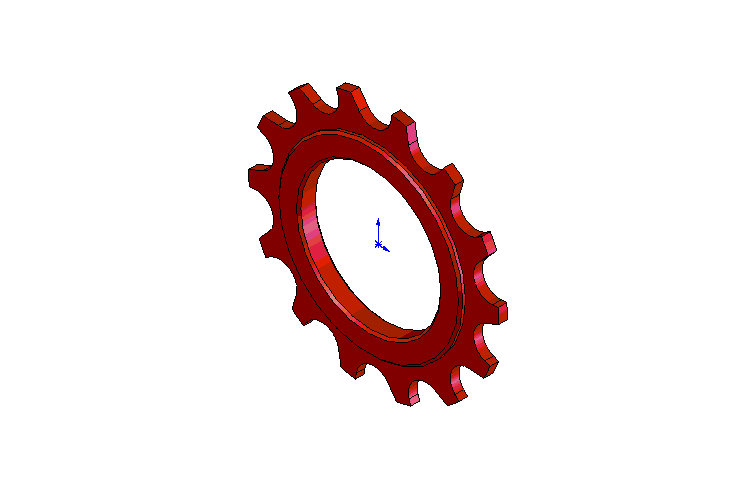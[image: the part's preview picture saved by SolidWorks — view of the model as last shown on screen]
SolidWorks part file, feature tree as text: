
SOLIDWORKS PART (.sldprt)
format: sldprt  version: not decoded by parser v0  size: 244,736 bytes
history: native  units: mm
features: sketch x4, plane x3, extrude x3, material x1, cut_extrude x1, pattern_circular x1, chamfer x1 (+10 scaffold rows collapsed)
feature tree (24):
  scaffold x10  (default folders/planes/origin — collapsed)
  material  "Matériau <non spécifié>"
  plane  "Plan de face"
  plane  "Plan de dessus"
  plane  "Plan de droite"
  sketch  "Esquisse1"  dims[D1=57.0mm]
  extrude  "Extrusion1"  Depth=2mm
  sketch  "Esquisse2"  dims[c1.D1=8.0mm c1.D3=4.0mm c2.D1=8.0mm c2.D3=4.0mm c2.D2=9.5mm c3.D3=4.0mm c3.D2=~2.039916mm c4.D2=35.0deg c4.D3=5.0mm]
  cut_extrude  "Enlèv. mat.-Extru.1"  [1 undecoded]
  pattern_circular  "Répétition circulaire1"  Count=14 Angle=25.714286deg
  sketch  "Esquisse3"  dims[D1=42.0mm]
  extrude  "Extrusion2"  Depth=4.25mm
  sketch  "Esquisse4"  dims[D1=32.0mm]
  extrude  "Enlèv. mat.-Extru.2"  [1 undecoded]
  chamfer  "Chanfrein1"  Distance=0.5mm Angle=45deg
decode coverage: 8 of 10 modeling features carry decoded parameters
note: ~ marks probable driven/reference dimensions
note: 2 parameter values undecoded
note: suppression state not decoded; provenance and decode notes live in map.json
